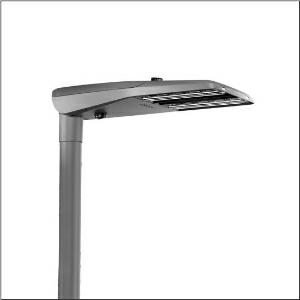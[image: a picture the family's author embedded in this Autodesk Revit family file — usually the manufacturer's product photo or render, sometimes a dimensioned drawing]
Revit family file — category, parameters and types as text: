
# Revit family: streetlight_sl_11_iq_midi___pc-r_5xc3f51y08me_63e7
name_source: partatom
category: Lighting Fixtures
units: mm (PartAtom-declared; Revit-internal decimal feet)

## family parameters
Cut with Voids When Loaded = No
Host = Face
Light Source = No
Part Type = Normal
Room Calculation Point = No
Round Connector Dimension = Use Diameter
Shared = No

## types (1)
- --- (1 x LED, 15540 lm, 122.7 W, 3000K)
    Apparent Load = 123 VA
    CIE Flux Codes = 37 73 96 100 100
    Color Rendering = 70
    Color Temperature = 3000K
    Default Elevation = 1800 mm
    Description = Streetlight SL 11 iQ midi, mast luminaire, primary light control with 3 zone facetted reflector, of plastic, silver coated, highly specular, primary optical cover: cover, of PMMA, transparent, light distribution: PC-R, light emission: direct distribution, primary light characteristic: asymmetric, right, installation type: post-top, side-entry, lamps: LED, High Power LED, rated values: 15.540lm | 122,7W | 126,7lm/W (begin service life); end service life: 15.540lm | 130,2W; at 50% lumin. flux: 7.770lm | 56,1W | 138,5lm/W, colour temperature: 3000K, colour rendering: CRI > 70, light colour: 730, light setting 1 begin service life: 100% | 15.540lm | 122,7W | 126,7lm/W | 3.000K, light setting 1 end service life: 130,2W, further light settings possible, control: pre-setting: logarithmic dimming characteristic, Street-Remote, Auto-Match, Temp-Guard, Lumen-Switch, Night-Set, Smart-Wire, Light-Fading, Desk-Remote (wireless, voltage-free reading and setting of iQ features in the workshop via application-optimized NFC function/RFID function), optimised constant luminous flux control (CLO 2.0), with cable H07RN-F 3x 1.5mm², mains connection: 230..240V, AC, 50/60Hz, connection cable pre-assembled, cable length: 12,5m, luminaire housing, of diecast aluminium, powder-coated, SITECO metallic grey (DB 702S), please order mast flange separately, inclination adjustable without tools: 0°, 5°, 10°, 15° (post-top) | 0°, -5°, -10°, -15° (side-entry), sealing non-destructively replaceable, multi-level sealing system, length: 780mm, width: 376mm, height: 118mm, mast flange for spigot size: 42mm (side-entry): 5XC10008XM4, 60/48mm (side-entry/post-top): 5XC10108XM2, 76/60mm (side-entry/post-top): 5XC10108XM1, equipment: Power, Smart Interface below and above, protection rating (complete): IP66, insulation class (complete): insulation class II (safety insulation), certification: CE, ENEC, ENEC+, VDE, UKCA, impact resistance: IK10, permissible operating ambient temperature for outdoor applications: -25..+50°C, standard-compliant lighting for roads and squares, Environmental Product Declaration (EPD) tested and certified by an independent institute, packaging unit: 1 piece

Light Distribution: PC-R
    Height = 118 mm
    Lamp = 1 x LED
    Lamp Light Flux = 15540 lm
    Lamp Power = 122.7 W
    Lamp count = 1
    Length = 780 mm
    Luminous efficacy = 127 lm/W
    Manufacturer = Siteco
    ModVariant = No
    Model = 5XC3F51Y08ME
    Number of Poles = 1
    OnlyDefault = Yes
    Power Factor = 1
    Product Name = Streetlight SL 11 iQ midi | PC-R
    Product group = mast luminaire | pylon top
    ProductGroupID = 6100
    Protection Class = Protection class II
    Protection Degree = IP 66
    RLX_Detail_Level = 1
    RLX_Emergency_Light_Flux = 0 lm
    RLX_Emergency_Type = 0
    RLX_Emergency_Type_DB = No
    RlxData = <blob elided: 73581 chars, md5=2cd8b5a5>
    Socket = socket
    Standby Power = 0 W
    System Light Flux = 15540 lm
    System Power = 123 W
    Type Comments = factory setting: luminous flux: 100 % | dim-lin: 254 | 552 mA
    Type Image = l_1004429.jpg
    URL = http://relux.com
    VarID = @adj_132499
    Voltage = 0 V
    Weight = 0.00 kg
    Width = 376 mm

## geometry (parser evidence)
native form markers: Blend x4, Sweep x11
no freeform markers — native parametric forms only
